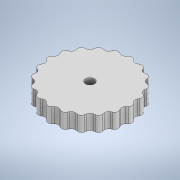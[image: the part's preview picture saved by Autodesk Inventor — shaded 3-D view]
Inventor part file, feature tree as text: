
AUTODESK INVENTOR PART (.ipt)
format: ipt  version: 2022 (Build 260153000, 153)  size: 276,480 bytes
history: native  units: in
note: dims shown in document units (in); Inventor stores cm internally (conversion verified against a paired STEP export)
features: extrude x4, sketch x4, projected_geometry x3, fillet x1
ambient origin geometry x8: Origin, YZ Plane, XZ Plane, XY Plane, X Axis, Y Axis, Z Axis, Center Point
bodies: Solid1 (feature_tree)
feature tree (12):
  extrude  "Extrusion1"  Depth=0.1181in
  extrude  "Extrusion3"  Depth=0.1181in
  extrude  "Extrusion4"  Depth=0.0591in
  extrude  "Extrusion5"  Depth=0.05in
  fillet  "Fillet1"  Radius=0.15in
  sketch  "Sketch1"  dims[d0=0.1181in d1=1.0in]
  sketch  "Sketch3"  dims[d2=0.1181in d3=0.0in d14=0.875in]
  sketch  "Sketch4"  dims[d15=0.0787in d16=0.0in d17=0.0591in]
  projected_geometry  "Projected Loop2"
  projected_geometry  "Projected Loop3"
  sketch  "Sketch5"  dims[d18=0.3in d19=0.05in d20=0.15in d21=0.05in d22=0.15in d23=0.0787in d24=0.0in d28=0.075in d29=45.0deg d30=135.0deg d31=7.874in d33=360.0deg d35=0.0787in d36=0.0in d37=0.275in d38=0.05in d39=0.15in d40=0.05in d41=135.0deg d42=0.05in]
  projected_geometry  "Projected Loop4"
